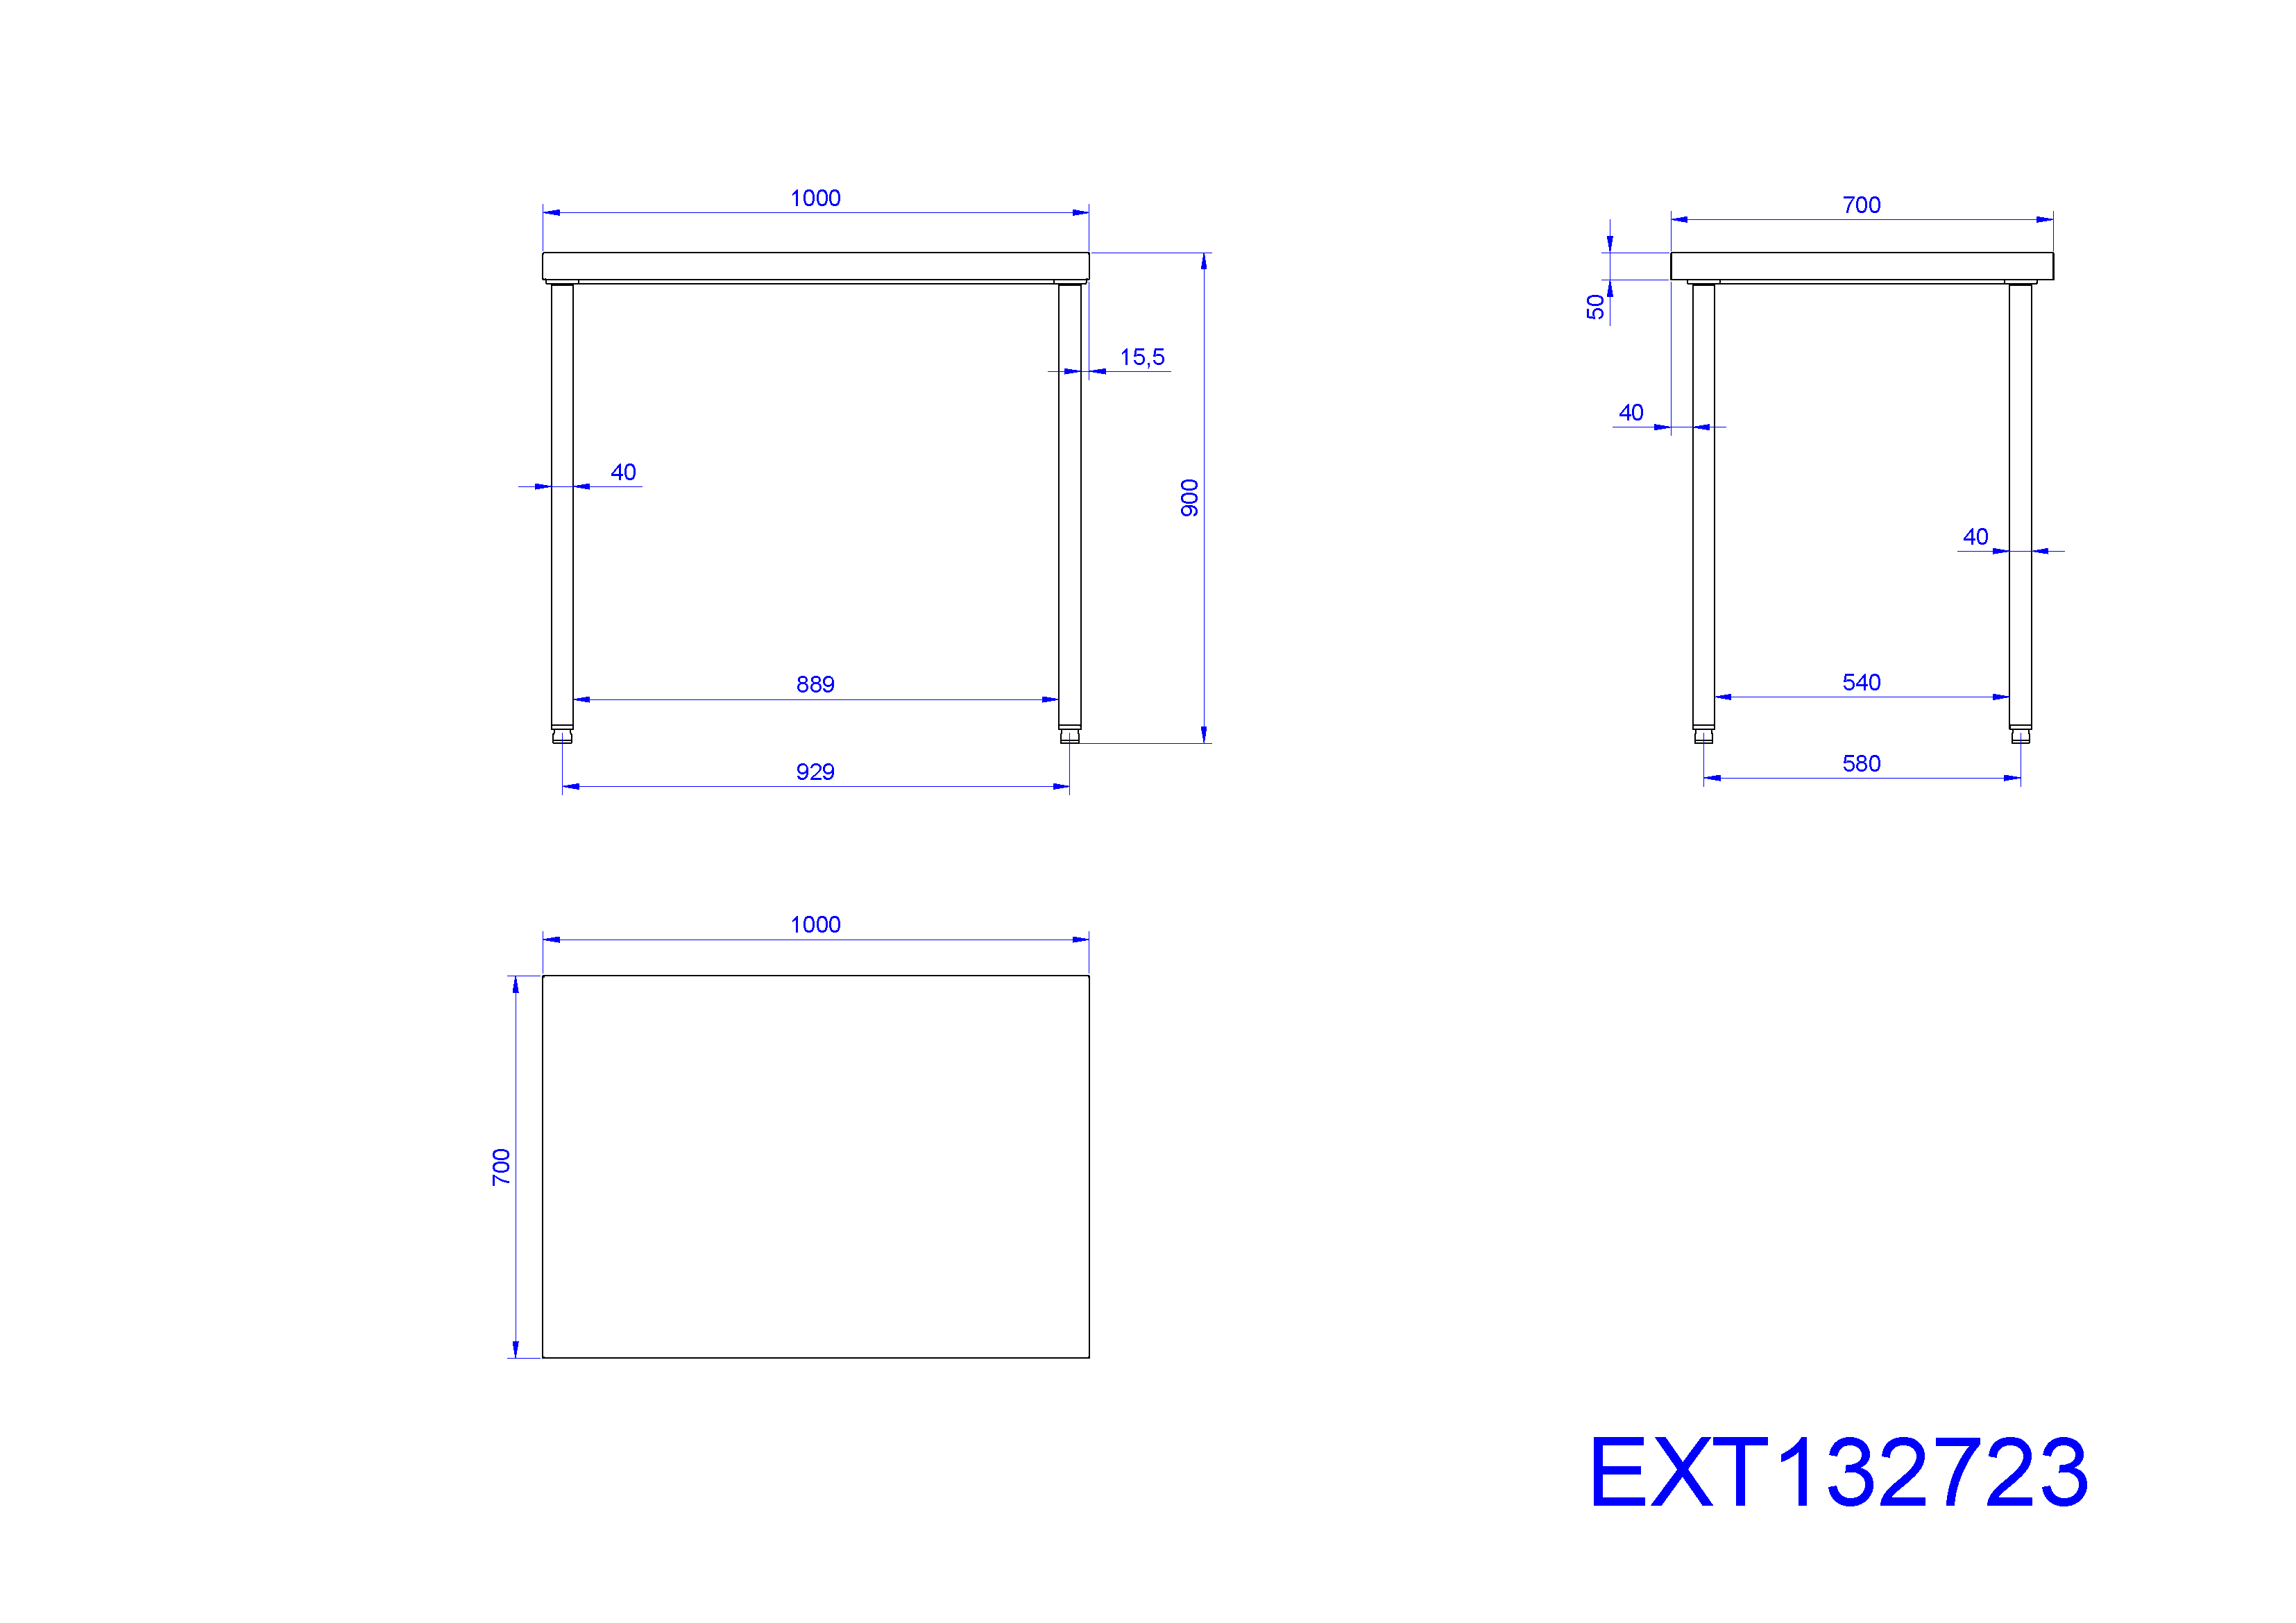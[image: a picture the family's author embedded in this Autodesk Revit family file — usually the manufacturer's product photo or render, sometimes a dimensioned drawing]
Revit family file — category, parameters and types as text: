
# Revit family: QF_ELECTROLUXPROFESSIONAL_132820_MLA1225PN
name_source: partatom
category: Attrezzature speciali
units: mm (PartAtom-declared; Revit-internal decimal feet)

## family parameters
Basato su piano di lavoro = No
Condiviso = No
Punto di calcolo locali = No
Quota connettore circolare = Usa diametro
Sempre verticale = Sì
Taglio con vuoti quando caricato = No
Tipo di parte = Normale

## types (1)
- Standard
    Accessory = Sì
    Cold Water Size = 0 mm
    Compressed Air Pressure = 0.0 Pa
    Compressed Air Size = 0 mm
    Compressed Air Volume = 0.0 L/s
    Condensate Return Size = 0 mm
    Cycle = 0 Hz
    Depth Actual = 700 mm  [stored 2.29659 ft]
    Descrizione = CUPBOARD SINK 2 BOWLS (500X500) 1200 MM
    Direct Waste Size = 51 mm
    Gas Input Pressure = 0
    Gas KW = 0
    Gas Size = 0 mm
    HP = 0 HP
    Height Actual = 1000 mm  [stored 3.28084 ft]
    Hot Water Size = 0 mm
    Item Number = 132820
    Length Actual = 1200 mm
    Modello = MLA1225PN
    Phase = 0
    Produttore = Electrolux Professional
    Prospetto di default = 0 mm  [stored 0 ft]
    Refrigerant Compressor Remote = Sì
    Refrigeration Liquid Line Size = 0 mm  [stored 0 ft]
    Refrigeration Suction Line Size = 0 mm  [stored 0 ft]
    Steam Consumption per Hour = 0
    Steam Supply Maximum Pressure = 0.0 Pa
    Steam Supply Minimum Pressure = 0.0 Pa
    Steam Supply Size = 0 mm
    URL = https://www.electroluxprofessional.com
    URL Manufacturer = https://www.electroluxprofessional.com
    Volts = 0 V
    Watts = 0 W
    Weight = 55.00 kg

note: source unit labels omitted for Gas Input Pressure — the stored unit's dimension contradicts the parameter name (converter mislabeling)

note: [stored X ft] marks values corroborated as IEEE doubles in the binary element streams (Revit-internal decimal feet)

## geometry (parser evidence)
native form markers: Sweep x4
no freeform markers — native parametric forms only
